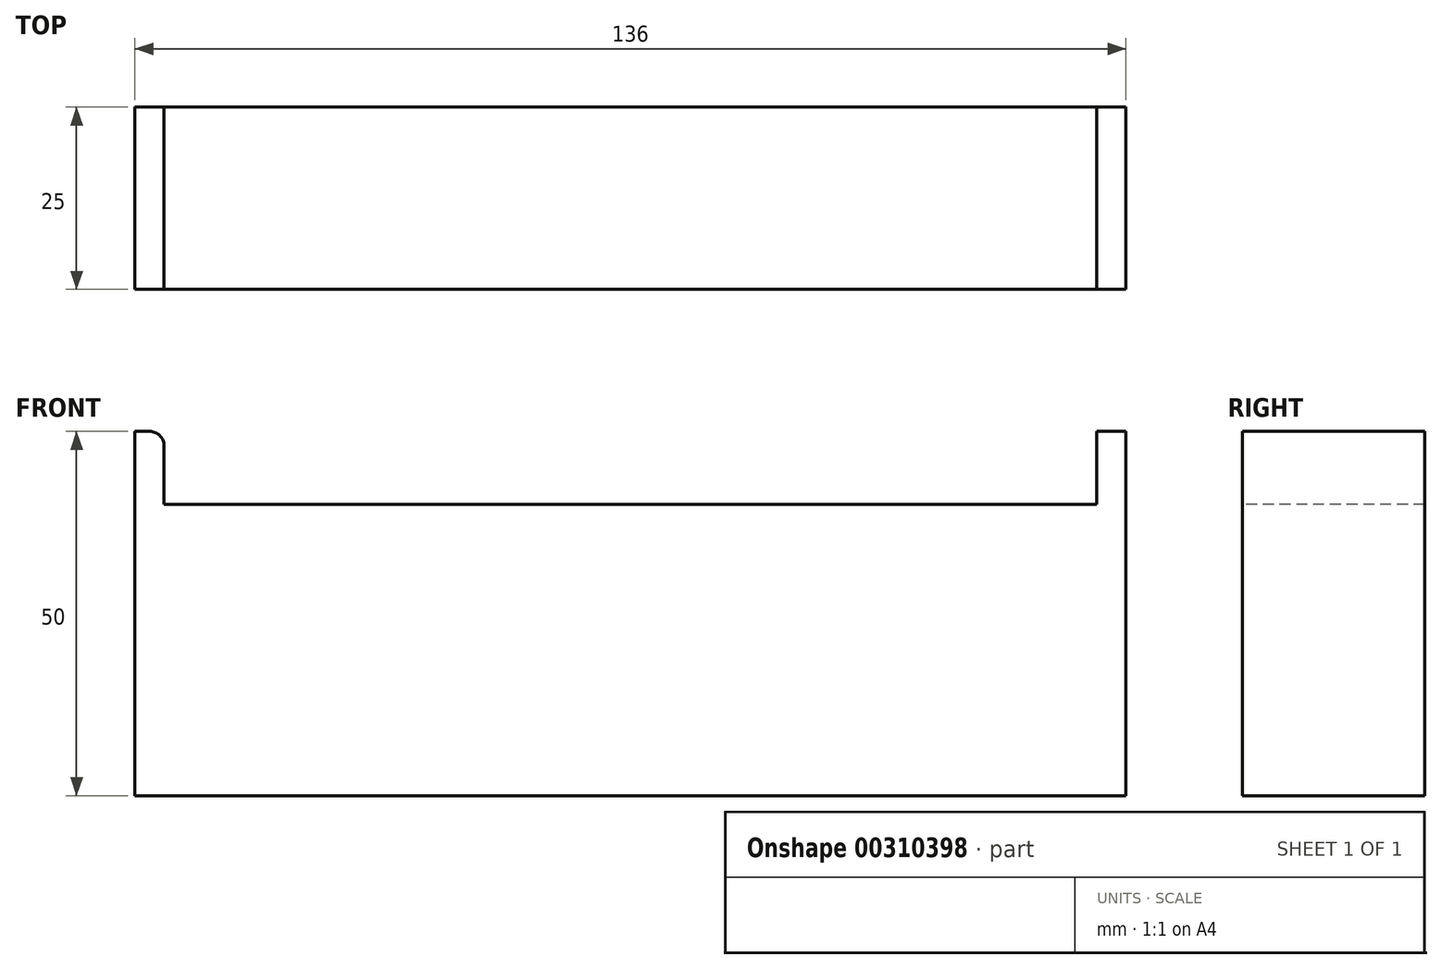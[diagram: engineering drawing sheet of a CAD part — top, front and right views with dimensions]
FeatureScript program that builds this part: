
annotation { "Feature Type Name" : "Feature", "Feature Type Description" : "" }
export const myFeature = defineFeature(function(context is Context, id is Id, definition is map)
    precondition{}
    {
        {
            var Q0;
            Q0=qCreatedBy(makeId("Front.planeOp"),FACE);
            var sketch = newSketch(context, id + "F0", { "sketchPlane" : qUnion([Q0])});
            skLineSegment(sketch, "E0.bottom", {"start": v(68, -25) * mm, "end": v(-68, -25) * mm});
            skLineSegment(sketch, "E0.top", {"start": v(68, 25) * mm, "end": v(-68, 25) * mm});
            skLineSegment(sketch, "E0.left", {"start": v(68, -25) * mm, "end": v(68, 25) * mm});
            skLineSegment(sketch, "E0.right", {"start": v(-68, -25) * mm, "end": v(-68, 25) * mm});
            skPoint(sketch, "E0.middle", {"position": v(0, 0) * mm});
            skSolve(sketch);
        }
        {
            var Q0;
            Q0 = qSketchRegion(id + "F0", true);
            extrude(context, id + "F1", {"entities" : qUnion([Q0]), "depth" : 25 * mm});
        }
        {
            var Q0;
            Q0=makeQuery(id+"F1.opExtrude","CAP_FACE",FACE,{"disambiguationData":[OSD([sQuery(id+"F0.wireOp",EDGE,"E0.bottom"),sQuery(id+"F0.wireOp",EDGE,"E0.top"),sQuery(id+"F0.wireOp",EDGE,"E0.left"),sQuery(id+"F0.wireOp",EDGE,"E0.right")])],"isStart":false});
            var sketch = newSketch(context, id + "F2", { "sketchPlane" : qUnion([Q0])});
            skLineSegment(sketch, "E1.bottom", {"start": v(-64, 25) * mm, "end": v(64, 25) * mm});
            skLineSegment(sketch, "E1.top", {"start": v(-64, 15) * mm, "end": v(64, 15) * mm});
            skLineSegment(sketch, "E1.left", {"start": v(-64, 25) * mm, "end": v(-64, 15) * mm});
            skLineSegment(sketch, "E1.right", {"start": v(64, 25) * mm, "end": v(64, 15) * mm});
            skSolve(sketch);
        }
        {
            var Q0;
            Q0 = qSketchRegion(id + "F2", true);
            extrude(context, id + "F3", {"entities" : qUnion([Q0]), "operationType" : NewBodyOperationType.REMOVE, "endBound" : BoundingType.THROUGH_ALL, "oppositeDirection" : true, "depth" : 25 * mm});
        }
        {
            var Q0;
            Q0=makeQuery(id+"F3.boolean.opBoolean","COPY",EDGE,{"derivedFrom":makeQuery(id+"F3.opExtrude","SWEPT_EDGE",EDGE,{"disambiguationData":[OSD([sQuery(id+"F0.wireOp",EDGE,"E0.top"),sQuery(id+"F2.wireOp",EDGE,"E1.bottom"),sQuery(id+"F2.wireOp",EDGE,"E1.left")])]})});
            var Q1;
            Q1=makeQuery(id+"F3.boolean.opBoolean","COPY",EDGE,{"derivedFrom":makeQuery(id+"F3.opExtrude","SWEPT_EDGE",EDGE,{"disambiguationData":[OSD([sQuery(id+"F0.wireOp",EDGE,"E0.top"),sQuery(id+"F2.wireOp",EDGE,"E1.bottom"),sQuery(id+"F2.wireOp",EDGE,"E1.right")])]})});
            fillet(context, id + "F4", {"entities" : qUnion([Q0, Q1]), "radius" : 2 * mm, "tangentPropagation" : true, "allowEdgeOverflow" : false});
        }
    });
